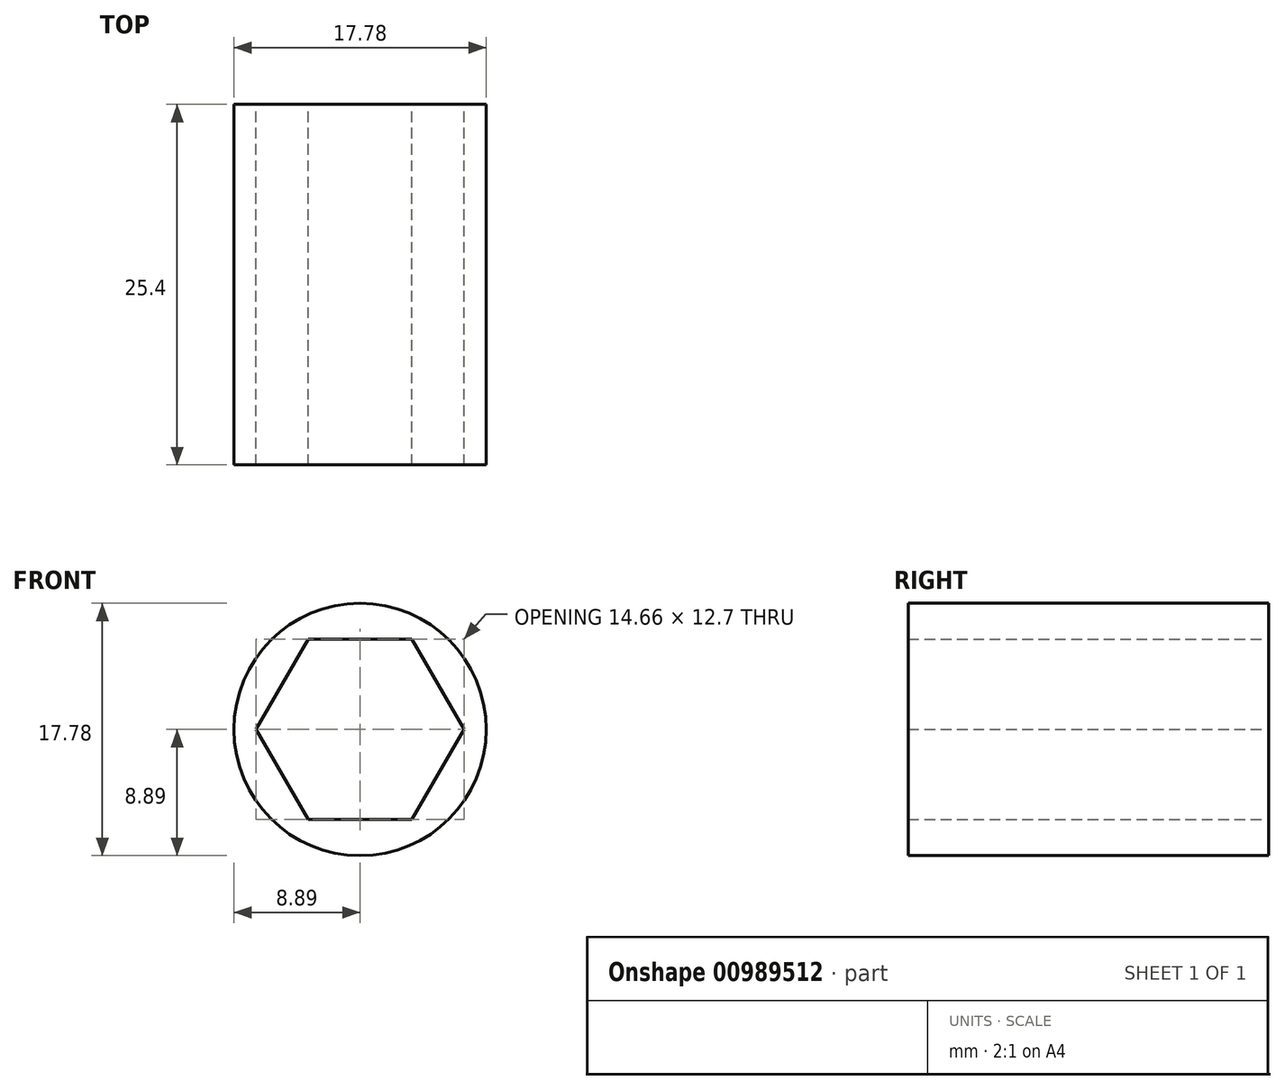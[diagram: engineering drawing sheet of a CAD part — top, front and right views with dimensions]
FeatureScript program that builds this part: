
annotation { "Feature Type Name" : "Feature", "Feature Type Description" : "" }
export const myFeature = defineFeature(function(context is Context, id is Id, definition is map)
    precondition{}
    {
        {
            var Q0;
            Q0=qCreatedBy(makeId("Front.planeOp"),FACE);
            var sketch = newSketch(context, id + "F0", { "sketchPlane" : qUnion([Q0])});
            skCircle(sketch, "E0", {"center": v(0, 0) * mm, "radius": 8.9 * mm});
            skCircle(sketch, "E1.cCircle", {"center": v(0, 0) * mm, "radius": 6.35 * mm, "construction": true});
            skLineSegment(sketch, "E1.0", {"start": v(-3.67, 6.35) * mm, "end": v(3.67, 6.35) * mm});
            skLineSegment(sketch, "E1.1", {"start": v(3.67, 6.35) * mm, "end": v(7.33, 0) * mm});
            skLineSegment(sketch, "E1.2", {"start": v(7.33, 0) * mm, "end": v(3.67, -6.35) * mm});
            skLineSegment(sketch, "E1.3", {"start": v(3.67, -6.35) * mm, "end": v(-3.67, -6.35) * mm});
            skLineSegment(sketch, "E1.4", {"start": v(-3.67, -6.35) * mm, "end": v(-7.33, 0) * mm});
            skLineSegment(sketch, "E1.5", {"start": v(-7.33, 0) * mm, "end": v(-3.67, 6.35) * mm});
            skPoint(sketch, "E1.0.midPoint", {"position": v(0, 6.35) * mm});
            skSolve(sketch);
        }
        {
            var Q0;
            Q0=qSketchRegion(id+"F0",true);
            extrude(context, id + "F1", {"entities" : qUnion([Q0]), "depth" : 25.4 * mm, "offsetDistance" : 25.4 * mm});
        }
    });
